# Revit family: Hekatron_Raumlufttechnik_RZA 142 AP_DE_22.01
name_source: partatom
category: Brandmelder
revit_build: Autodesk Revit 2018 (Build: 20190510_1515(x64)
units: mm (PartAtom-declared; Revit-internal decimal feet)

## family parameters
Basisbauteil = Fläche
Beim Laden mit Abzugskörper schneiden = Nein
Bemaßung runder Anschluss = Durchmesser verwenden
Beschriftungsausrichtung beibehalten = Ja
Gemeinsam genutzt = Nein
OmniClass-Nummer = 23.85.30.21
OmniClass-Titel = Environmental Detection/Registration
Raumberechnungspunkt = Nein
Teiletyp = Normal

## types (1)
- RZA 142 AP
    Beschreibung = Fernanzeigetableau für Rauch- und Thermoschalter mit 5 farbigen LED zur Zu standsanzeige der angeschlos- senen Rauchschalter, Aufputz-Montage
    Betriebsspannung = 18 bis 28 V
    Breite (mm) = 29.5
    Farbe = weiß, ähnlich RAL 9010
    Hersteller = Hekatron
    Höhe (mm) = 117.0
    Kabeleinführung = oben, unten, seitlich, hinten
    Link zu Ausschreibungstext = https://www.meinhplus.de
    Link zu Produktinformation = https://www.hekatron-planungstools.de
    Link zu ausschreiben.de = http://www.ausschreiben.de
    Link zum Datenblatt = https://www.hekatron-planungstools.de
    Material = ABS
    Modell = RZA 142 AP
    Montageart = Aufputz
    Nettogewicht (g) = 185.0
    Schutzart = IP 42
    Stromaufnahme = max. 120mA
    Tiefe (mm) = 117.0
    Typenkommentare = Rauchschalterzustandsanzeige Aufputz
    UB A&S Artikel Nummer = 5500034
    URL = https://www.hekatron-brandschutz.de
    Version des BIM Objektes = 22.01
    Vorgabe-Ansicht = 1200 mm
    Zulässige Umgebungstemperatur = -20 °C bis +70 °C

## geometry (parser evidence)
native form markers: Extrusion x1, Sweep x2
no freeform markers — native parametric forms only
